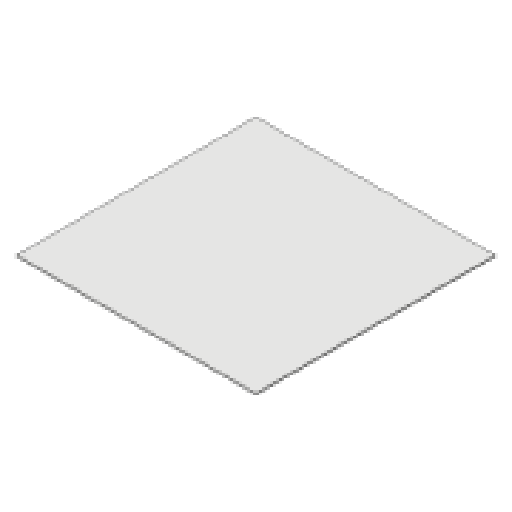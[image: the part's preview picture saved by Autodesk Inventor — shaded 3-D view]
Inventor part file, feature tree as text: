
AUTODESK INVENTOR PART (.ipt)
format: ipt  version: 2025.1 (Build 291241000, 241)  size: 80,384 bytes
history: native  units: mm
features: other x1, extrude x1, sketch x1
ambient origin geometry x8: Origin, YZ Plane, XZ Plane, XY Plane, X Axis, Y Axis, Z Axis, Center Point
bodies: Body1 (feature_tree)
feature tree (3):
  other  "Bryła1"
  extrude  "Wyciągnięcie proste1"  Depth=1500.0mm
  sketch  "Szkic1"
